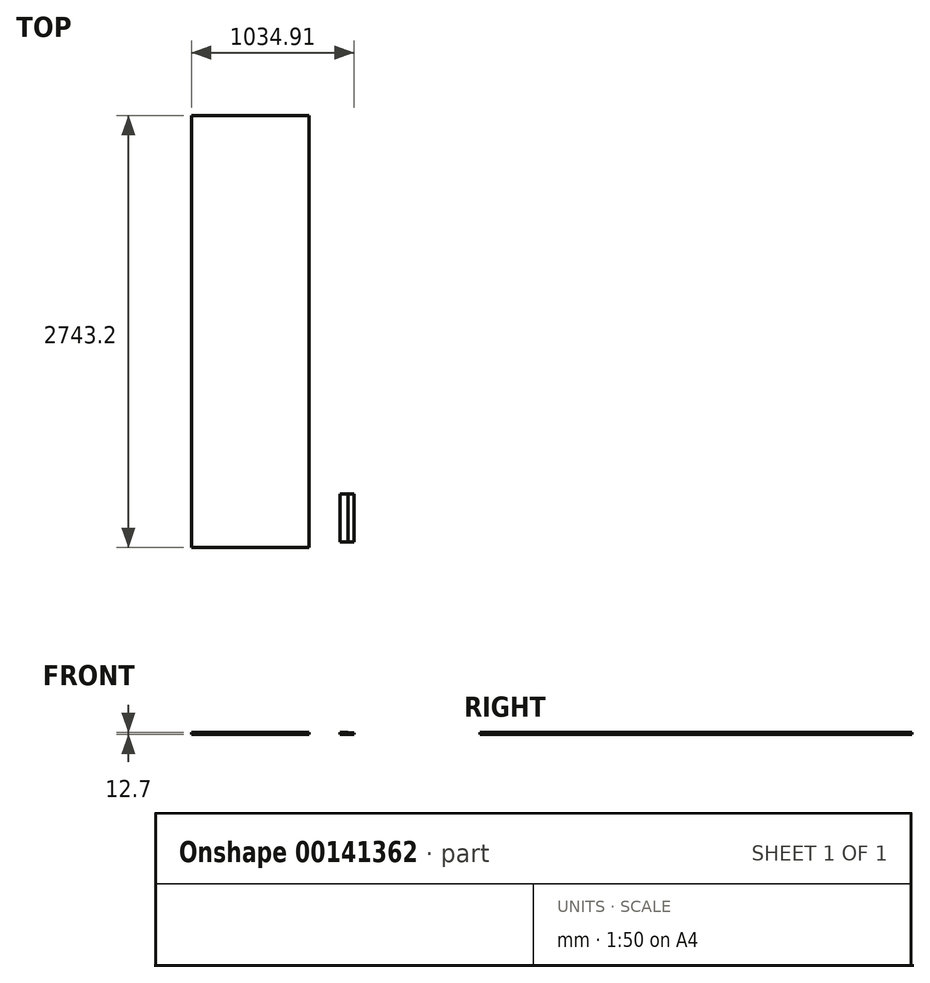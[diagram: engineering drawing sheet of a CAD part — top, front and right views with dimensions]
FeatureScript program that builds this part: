
annotation { "Feature Type Name" : "Feature", "Feature Type Description" : "" }
export const myFeature = defineFeature(function(context is Context, id is Id, definition is map)
    precondition{}
    {
        {
            var Q0;
            Q0=qCreatedBy(makeId("Top.planeOp"),FACE);
            var sketch = newSketch(context, id + "F0", { "sketchPlane" : qUnion([Q0])});
            skLineSegment(sketch, "E0.bottom", {"start": v(-1246.62, 2708.73) * mm, "end": v(-497.32, 2708.73) * mm});
            skLineSegment(sketch, "E0.top", {"start": v(-1246.62, -34.47) * mm, "end": v(-497.32, -34.47) * mm});
            skLineSegment(sketch, "E0.left", {"start": v(-1246.62, 2708.73) * mm, "end": v(-1246.62, -34.47) * mm});
            skLineSegment(sketch, "E0.right", {"start": v(-497.32, 2708.73) * mm, "end": v(-497.32, -34.47) * mm});
            skSolve(sketch);
        }
        {
            var Q0;
            Q0=qSketchRegion(id+"F0",true);
            extrude(context, id + "F1", {"entities" : qUnion([Q0]), "depth" : 12.7 * mm});
        }
        {
            var Q0;
            Q0=qCreatedBy(makeId("Top.planeOp"),FACE);
            var sketch = newSketch(context, id + "F2", { "sketchPlane" : qUnion([Q0])});
            skLineSegment(sketch, "E1.bottom", {"start": v(-211.7, 0) * mm, "end": v(-300.6, 0) * mm});
            skLineSegment(sketch, "E1.top", {"start": v(-211.7, 304.8) * mm, "end": v(-300.6, 304.8) * mm});
            skLineSegment(sketch, "E1.left", {"start": v(-211.7, 0) * mm, "end": v(-211.7, 304.8) * mm});
            skLineSegment(sketch, "E1.right", {"start": v(-300.6, 0) * mm, "end": v(-300.6, 304.8) * mm});
            skSolve(sketch);
        }
        {
            var Q0;
            Q0=makeQuery(id+"F2.imprint","IMPRINT",FACE,{"disambiguationData":[TD([[makeQuery(id+"F2.imprint","IMPRINT",EDGE,{"derivedFrom":sQuery(id+"F2.wireOp",EDGE,"E1.bottom")}),-1.0]])]});
            extrude(context, id + "F3", {"entities" : qUnion([Q0]), "depth" : 12.7 * mm});
        }
        {
            var Q0;
            Q0=makeQuery(id+"F3.opExtrude","CAP_FACE",FACE,{"disambiguationData":[OSD([sQuery(id+"F2.wireOp",EDGE,"E1.bottom"),sQuery(id+"F2.wireOp",EDGE,"E1.top"),sQuery(id+"F2.wireOp",EDGE,"E1.left"),sQuery(id+"F2.wireOp",EDGE,"E1.right")])],"isStart":false});
            var sketch = newSketch(context, id + "F4", { "sketchPlane" : qUnion([Q0])});
            skLineSegment(sketch, "E2.bottom", {"start": v(-211.7, 0) * mm, "end": v(-249.8, 0) * mm});
            skLineSegment(sketch, "E2.top", {"start": v(-211.7, 304.8) * mm, "end": v(-249.8, 304.8) * mm});
            skLineSegment(sketch, "E2.left", {"start": v(-211.7, 0) * mm, "end": v(-211.7, 304.8) * mm});
            skLineSegment(sketch, "E2.right", {"start": v(-249.8, 0) * mm, "end": v(-249.8, 304.8) * mm});
            skSolve(sketch);
        }
        {
            var Q0;
            Q0 = qSketchRegion(id + "F4", true);
            extrude(context, id + "F5", {"entities" : qUnion([Q0]), "operationType" : NewBodyOperationType.REMOVE, "oppositeDirection" : true, "depth" : 3.17 * mm});
        }
    });
